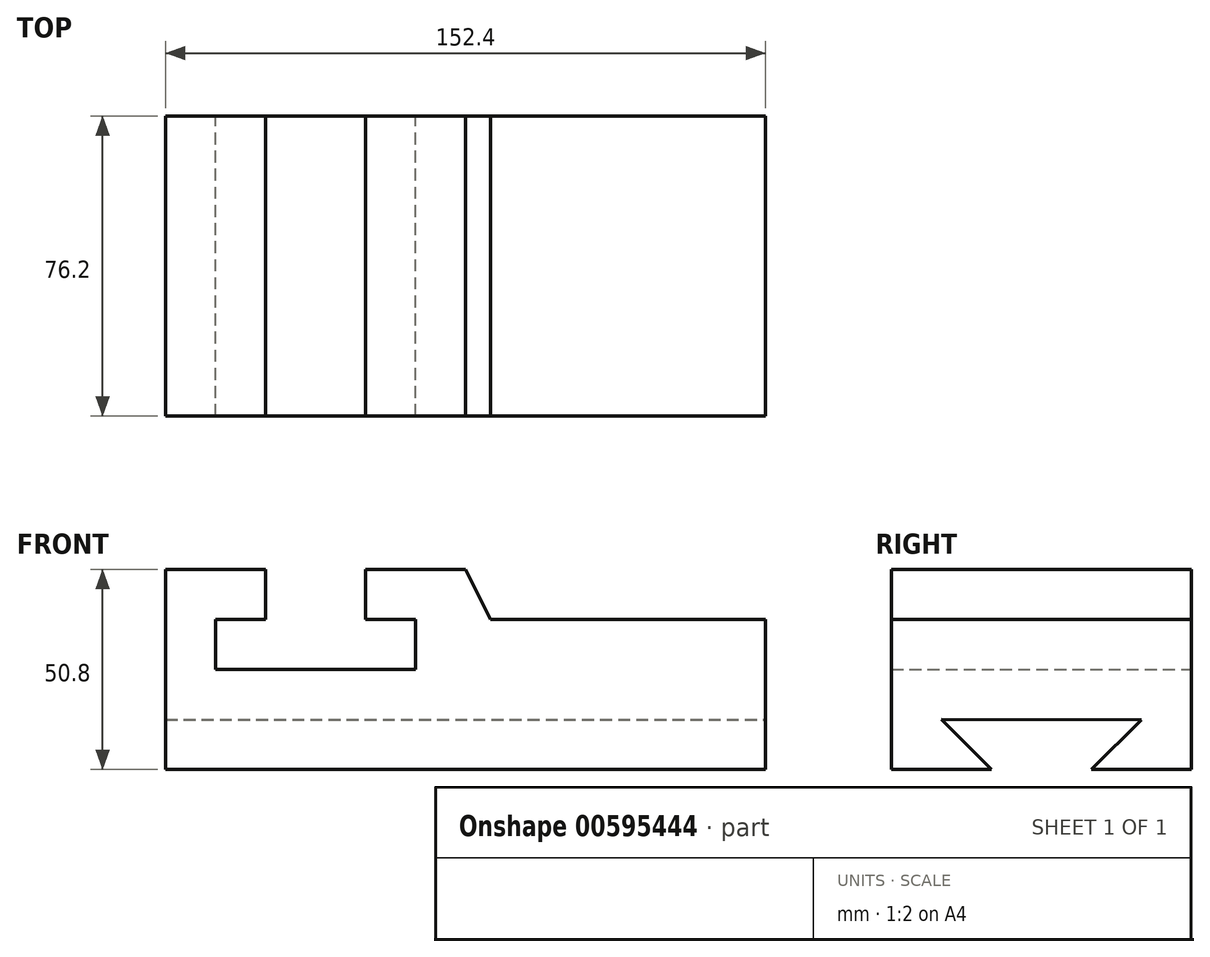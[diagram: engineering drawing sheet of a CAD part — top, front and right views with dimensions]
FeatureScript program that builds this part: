
annotation { "Feature Type Name" : "Feature", "Feature Type Description" : "" }
export const myFeature = defineFeature(function(context is Context, id is Id, definition is map)
    precondition{}
    {
        {
            var Q0;
            Q0=qCreatedBy(makeId("Front.planeOp"),FACE);
            var sketch = newSketch(context, id + "F0", { "sketchPlane" : qUnion([Q0])});
            skLineSegment(sketch, "E0.bottom", {"start": v(0, 0) * mm, "end": v(152.4, 0) * mm});
            skLineSegment(sketch, "E0.left", {"start": v(0, 0) * mm, "end": v(0, 50.8) * mm});
            skLineSegment(sketch, "E1", {"start": v(0, 50.8) * mm, "end": v(25.4, 50.8) * mm});
            skLineSegment(sketch, "E2", {"start": v(25.4, 50.8) * mm, "end": v(25.4, 38.1) * mm});
            skLineSegment(sketch, "E3", {"start": v(25.4, 38.1) * mm, "end": v(12.7, 38.1) * mm});
            skLineSegment(sketch, "E4", {"start": v(12.7, 38.1) * mm, "end": v(12.7, 25.4) * mm});
            skLineSegment(sketch, "E5", {"start": v(12.7, 25.4) * mm, "end": v(63.5, 25.4) * mm});
            skLineSegment(sketch, "E6", {"start": v(63.5, 25.4) * mm, "end": v(63.5, 38.1) * mm});
            skLineSegment(sketch, "E7", {"start": v(63.5, 38.1) * mm, "end": v(50.8, 38.1) * mm});
            skLineSegment(sketch, "E8", {"start": v(50.8, 38.1) * mm, "end": v(50.8, 50.8) * mm});
            skLineSegment(sketch, "E9", {"start": v(50.8, 50.8) * mm, "end": v(76.2, 50.8) * mm});
            skLineSegment(sketch, "E10", {"start": v(82.55, 38.1) * mm, "end": v(76.2, 50.8) * mm});
            skLineSegment(sketch, "E11", {"start": v(82.55, 38.1) * mm, "end": v(152.4, 38.1) * mm});
            skLineSegment(sketch, "E12", {"start": v(152.4, 0) * mm, "end": v(152.4, 38.1) * mm});
            skSolve(sketch);
        }
        {
            var Q0;
            Q0 = qSketchRegion(id + "F0", true);
            extrude(context, id + "F1", {"entities" : qUnion([Q0]), "depth" : 76.2 * mm, "offsetDistance" : 25.4 * mm});
        }
        {
            var Q0;
            Q0=makeQuery(id+"F1.opExtrude","SWEPT_FACE",FACE,{"disambiguationData":[OSD([sQuery(id+"F0.wireOp",EDGE,"E12")])]});
            var sketch = newSketch(context, id + "F2", { "sketchPlane" : qUnion([Q0])});
            skLineSegment(sketch, "E13", {"start": v(-76.2, 0) * mm, "end": v(-50.8, 0) * mm});
            skLineSegment(sketch, "E14", {"start": v(-50.8, 0) * mm, "end": v(-25.4, 0) * mm});
            skLineSegment(sketch, "E15", {"start": v(0, 0) * mm, "end": v(-12.7, 0) * mm});
            skLineSegment(sketch, "E16", {"start": v(-12.7, 12.55) * mm, "end": v(-63.5, 12.7) * mm});
            skLineSegment(sketch, "E17", {"start": v(-50.8, 0) * mm, "end": v(-63.5, 12.7) * mm});
            skLineSegment(sketch, "E18", {"start": v(-25.4, 0) * mm, "end": v(-12.7, 12.55) * mm});
            skSolve(sketch);
        }
        {
            var Q0;
            Q0 = qSketchRegion(id + "F2", true);
            extrude(context, id + "F3", {"entities" : qUnion([Q0]), "operationType" : NewBodyOperationType.REMOVE, "oppositeDirection" : true, "depth" : 152.4 * mm, "offsetDistance" : 25.4 * mm});
        }
    });
